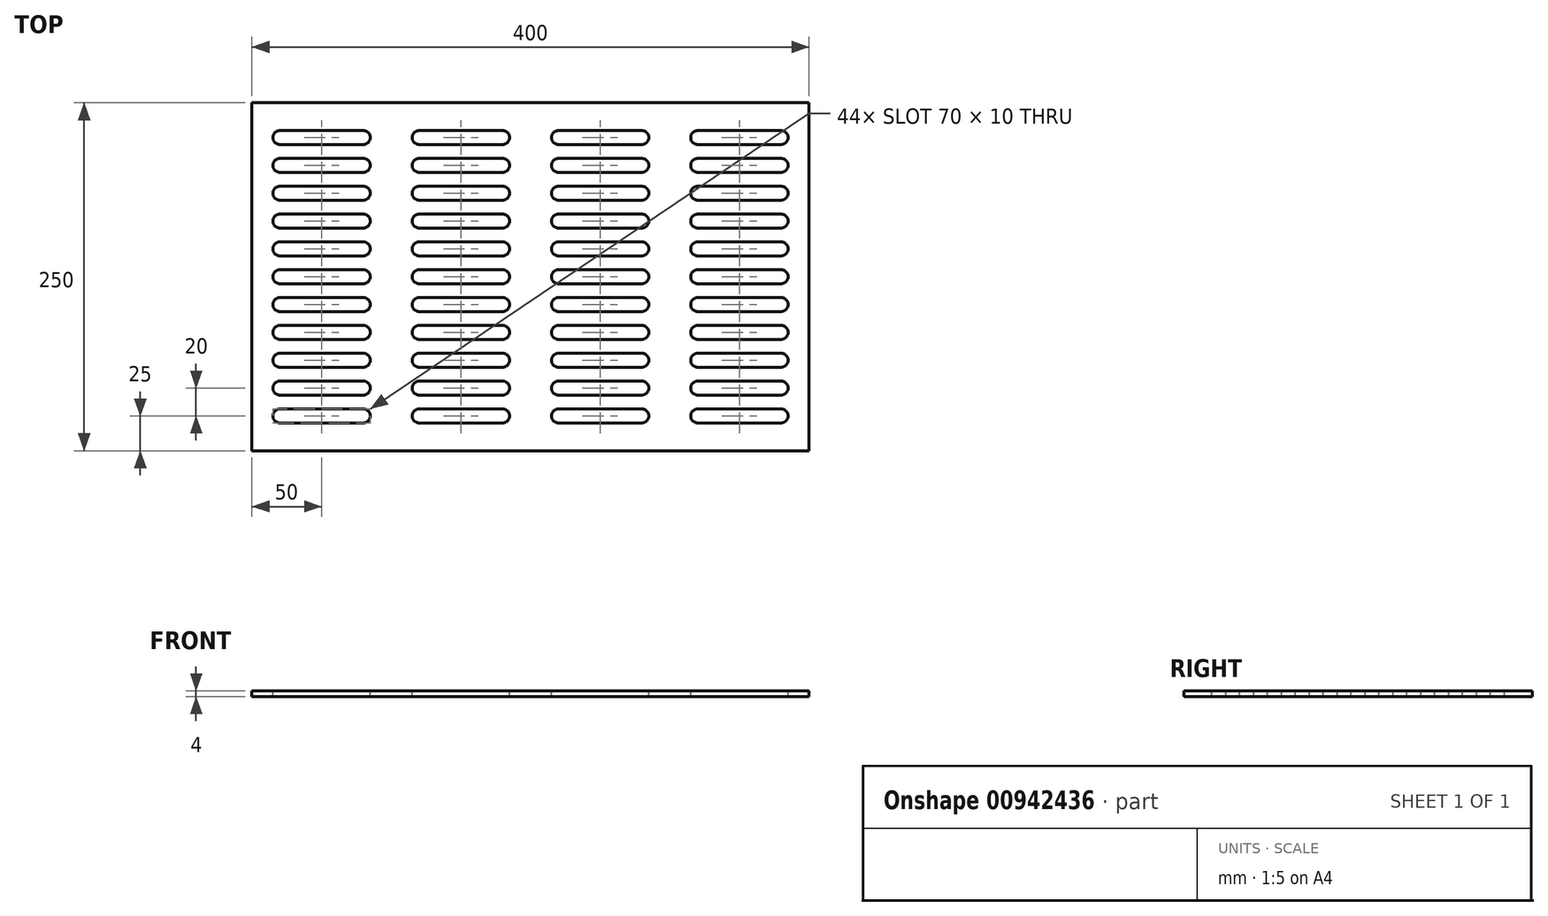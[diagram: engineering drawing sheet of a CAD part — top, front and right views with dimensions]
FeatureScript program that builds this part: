
annotation { "Feature Type Name" : "Feature", "Feature Type Description" : "" }
export const myFeature = defineFeature(function(context is Context, id is Id, definition is map)
    precondition{}
    {
        {
            var Q0;
            Q0=qCreatedBy(makeId("Top.planeOp"),FACE);
            var sketch = newSketch(context, id + "F0", { "sketchPlane" : qUnion([Q0])});
            skLineSegment(sketch, "E0.bottom", {"start": v(-200, 125) * mm, "end": v(200, 125) * mm});
            skLineSegment(sketch, "E0.top", {"start": v(-200, -125) * mm, "end": v(200, -125) * mm});
            skLineSegment(sketch, "E0.left", {"start": v(-200, 125) * mm, "end": v(-200, -125) * mm});
            skLineSegment(sketch, "E0.right", {"start": v(200, 125) * mm, "end": v(200, -125) * mm});
            skSolve(sketch);
        }
        {
            var Q0;
            Q0 = qSketchRegion(id + "F0", true);
            extrude(context, id + "F1", {"entities" : qUnion([Q0]), "depth" : 4 * mm, "offsetDistance" : 25 * mm});
        }
        {
            var Q0;
            Q0=makeQuery(id+"F1.opExtrude","CAP_FACE",FACE,{"disambiguationData":[OSD([sQuery(id+"F0.wireOp",EDGE,"E0.bottom"),sQuery(id+"F0.wireOp",EDGE,"E0.top"),sQuery(id+"F0.wireOp",EDGE,"E0.left"),sQuery(id+"F0.wireOp",EDGE,"E0.right")])],"isStart":false});
            var sketch = newSketch(context, id + "F2", { "sketchPlane" : qUnion([Q0])});
            skCircle(sketch, "E1", {"center": v(25, 80) * mm, "radius": 5 * mm});
            skCircle(sketch, "E2", {"center": v(25, -80) * mm, "radius": 5 * mm});
            skLineSegment(sketch, "E3.bottom", {"start": v(-180, 95) * mm, "end": v(105, 95) * mm});
            skLineSegment(sketch, "E3.top", {"start": v(-180, -95) * mm, "end": v(105, -95) * mm});
            skLineSegment(sketch, "E3.left", {"start": v(-180, 95) * mm, "end": v(-180, -95) * mm});
            skLineSegment(sketch, "E3.right", {"start": v(105, 95) * mm, "end": v(105, -95) * mm});
            skSolve(sketch);
        }
        {
            var Q0;
            Q0=makeQuery(id+"F2.imprint","IMPRINT",FACE,{"disambiguationData":[TD([[makeQuery(id+"F2.imprint","IMPRINT",EDGE,{"derivedFrom":sQuery(id+"F2.wireOp",EDGE,"E1")}),-1.0]])]});
            var sketch = newSketch(context, id + "F3", { "sketchPlane" : qUnion([Q0])});
            skLineSegment(sketch, "E4.bottom", {"start": v(120, 105) * mm, "end": v(180, 105) * mm});
            skLineSegment(sketch, "E4.top", {"start": v(120, 95) * mm, "end": v(180, 95) * mm});
            skArc(sketch, "E5", {"start": v(120, 105) * mm, "mid": v(115, 100) * mm, "end": v(120, 95) * mm});
            skArc(sketch, "E6", {"start": v(180, 95) * mm, "mid": v(185, 100) * mm, "end": v(180, 105) * mm});
            skArc(sketch, "E7.0.1.0", {"start": v(120, 85) * mm, "mid": v(115, 80) * mm, "end": v(120, 75) * mm});
            skLineSegment(sketch, "E7.0.1.1", {"start": v(120, 85) * mm, "end": v(180, 85) * mm});
            skLineSegment(sketch, "E7.0.1.2", {"start": v(120, 75) * mm, "end": v(180, 75) * mm});
            skArc(sketch, "E7.0.1.3", {"start": v(180, 75) * mm, "mid": v(185, 80) * mm, "end": v(180, 85) * mm});
            skArc(sketch, "E7.0.2.0", {"start": v(120, 65) * mm, "mid": v(115, 60) * mm, "end": v(120, 55) * mm});
            skLineSegment(sketch, "E7.0.2.1", {"start": v(120, 65) * mm, "end": v(180, 65) * mm});
            skLineSegment(sketch, "E7.0.2.2", {"start": v(120, 55) * mm, "end": v(180, 55) * mm});
            skArc(sketch, "E7.0.2.3", {"start": v(180, 55) * mm, "mid": v(185, 60) * mm, "end": v(180, 65) * mm});
            skArc(sketch, "E7.0.3.0", {"start": v(120, 45) * mm, "mid": v(115, 40) * mm, "end": v(120, 35) * mm});
            skLineSegment(sketch, "E7.0.3.1", {"start": v(120, 45) * mm, "end": v(180, 45) * mm});
            skLineSegment(sketch, "E7.0.3.2", {"start": v(120, 35) * mm, "end": v(180, 35) * mm});
            skArc(sketch, "E7.0.3.3", {"start": v(180, 35) * mm, "mid": v(185, 40) * mm, "end": v(180, 45) * mm});
            skArc(sketch, "E7.0.4.0", {"start": v(120, 25) * mm, "mid": v(115, 20) * mm, "end": v(120, 15) * mm});
            skLineSegment(sketch, "E7.0.4.1", {"start": v(120, 25) * mm, "end": v(180, 25) * mm});
            skLineSegment(sketch, "E7.0.4.2", {"start": v(120, 15) * mm, "end": v(180, 15) * mm});
            skArc(sketch, "E7.0.4.3", {"start": v(180, 15) * mm, "mid": v(185, 20) * mm, "end": v(180, 25) * mm});
            skArc(sketch, "E7.0.5.0", {"start": v(120, 5) * mm, "mid": v(115, 0) * mm, "end": v(120, -5) * mm});
            skLineSegment(sketch, "E7.0.5.1", {"start": v(120, 5) * mm, "end": v(180, 5) * mm});
            skLineSegment(sketch, "E7.0.5.2", {"start": v(120, -5) * mm, "end": v(180, -5) * mm});
            skArc(sketch, "E7.0.5.3", {"start": v(180, -5) * mm, "mid": v(185, 0) * mm, "end": v(180, 5) * mm});
            skArc(sketch, "E7.0.6.0", {"start": v(120, -15) * mm, "mid": v(115, -20) * mm, "end": v(120, -25) * mm});
            skLineSegment(sketch, "E7.0.6.1", {"start": v(120, -15) * mm, "end": v(180, -15) * mm});
            skLineSegment(sketch, "E7.0.6.2", {"start": v(120, -25) * mm, "end": v(180, -25) * mm});
            skArc(sketch, "E7.0.6.3", {"start": v(180, -25) * mm, "mid": v(185, -20) * mm, "end": v(180, -15) * mm});
            skArc(sketch, "E7.0.7.0", {"start": v(120, -35) * mm, "mid": v(115, -40) * mm, "end": v(120, -45) * mm});
            skLineSegment(sketch, "E7.0.7.1", {"start": v(120, -35) * mm, "end": v(180, -35) * mm});
            skLineSegment(sketch, "E7.0.7.2", {"start": v(120, -45) * mm, "end": v(180, -45) * mm});
            skArc(sketch, "E7.0.7.3", {"start": v(180, -45) * mm, "mid": v(185, -40) * mm, "end": v(180, -35) * mm});
            skArc(sketch, "E7.0.8.0", {"start": v(120, -55) * mm, "mid": v(115, -60) * mm, "end": v(120, -65) * mm});
            skLineSegment(sketch, "E7.0.8.1", {"start": v(120, -55) * mm, "end": v(180, -55) * mm});
            skLineSegment(sketch, "E7.0.8.2", {"start": v(120, -65) * mm, "end": v(180, -65) * mm});
            skArc(sketch, "E7.0.8.3", {"start": v(180, -65) * mm, "mid": v(185, -60) * mm, "end": v(180, -55) * mm});
            skArc(sketch, "E7.1.0.0", {"start": v(20, 105) * mm, "mid": v(15, 100) * mm, "end": v(20, 95) * mm});
            skLineSegment(sketch, "E7.1.0.1", {"start": v(20, 105) * mm, "end": v(80, 105) * mm});
            skLineSegment(sketch, "E7.1.0.2", {"start": v(20, 95) * mm, "end": v(80, 95) * mm});
            skArc(sketch, "E7.1.0.3", {"start": v(80, 95) * mm, "mid": v(85, 100) * mm, "end": v(80, 105) * mm});
            skArc(sketch, "E7.1.1.0", {"start": v(20, 85) * mm, "mid": v(15, 80) * mm, "end": v(20, 75) * mm});
            skLineSegment(sketch, "E7.1.1.1", {"start": v(20, 85) * mm, "end": v(80, 85) * mm});
            skLineSegment(sketch, "E7.1.1.2", {"start": v(20, 75) * mm, "end": v(80, 75) * mm});
            skArc(sketch, "E7.1.1.3", {"start": v(80, 75) * mm, "mid": v(85, 80) * mm, "end": v(80, 85) * mm});
            skArc(sketch, "E7.1.2.0", {"start": v(20, 65) * mm, "mid": v(15, 60) * mm, "end": v(20, 55) * mm});
            skLineSegment(sketch, "E7.1.2.1", {"start": v(20, 65) * mm, "end": v(80, 65) * mm});
            skLineSegment(sketch, "E7.1.2.2", {"start": v(20, 55) * mm, "end": v(80, 55) * mm});
            skArc(sketch, "E7.1.2.3", {"start": v(80, 55) * mm, "mid": v(85, 60) * mm, "end": v(80, 65) * mm});
            skArc(sketch, "E7.1.3.0", {"start": v(20, 45) * mm, "mid": v(15, 40) * mm, "end": v(20, 35) * mm});
            skLineSegment(sketch, "E7.1.3.1", {"start": v(20, 45) * mm, "end": v(80, 45) * mm});
            skLineSegment(sketch, "E7.1.3.2", {"start": v(20, 35) * mm, "end": v(80, 35) * mm});
            skArc(sketch, "E7.1.3.3", {"start": v(80, 35) * mm, "mid": v(85, 40) * mm, "end": v(80, 45) * mm});
            skArc(sketch, "E7.1.4.0", {"start": v(20, 25) * mm, "mid": v(15, 20) * mm, "end": v(20, 15) * mm});
            skLineSegment(sketch, "E7.1.4.1", {"start": v(20, 25) * mm, "end": v(80, 25) * mm});
            skLineSegment(sketch, "E7.1.4.2", {"start": v(20, 15) * mm, "end": v(80, 15) * mm});
            skArc(sketch, "E7.1.4.3", {"start": v(80, 15) * mm, "mid": v(85, 20) * mm, "end": v(80, 25) * mm});
            skArc(sketch, "E7.1.5.0", {"start": v(20, 5) * mm, "mid": v(15, 0) * mm, "end": v(20, -5) * mm});
            skLineSegment(sketch, "E7.1.5.1", {"start": v(20, 5) * mm, "end": v(80, 5) * mm});
            skLineSegment(sketch, "E7.1.5.2", {"start": v(20, -5) * mm, "end": v(80, -5) * mm});
            skArc(sketch, "E7.1.5.3", {"start": v(80, -5) * mm, "mid": v(85, 0) * mm, "end": v(80, 5) * mm});
            skArc(sketch, "E7.1.6.0", {"start": v(20, -15) * mm, "mid": v(15, -20) * mm, "end": v(20, -25) * mm});
            skLineSegment(sketch, "E7.1.6.1", {"start": v(20, -15) * mm, "end": v(80, -15) * mm});
            skLineSegment(sketch, "E7.1.6.2", {"start": v(20, -25) * mm, "end": v(80, -25) * mm});
            skArc(sketch, "E7.1.6.3", {"start": v(80, -25) * mm, "mid": v(85, -20) * mm, "end": v(80, -15) * mm});
            skArc(sketch, "E7.1.7.0", {"start": v(20, -35) * mm, "mid": v(15, -40) * mm, "end": v(20, -45) * mm});
            skLineSegment(sketch, "E7.1.7.1", {"start": v(20, -35) * mm, "end": v(80, -35) * mm});
            skLineSegment(sketch, "E7.1.7.2", {"start": v(20, -45) * mm, "end": v(80, -45) * mm});
            skArc(sketch, "E7.1.7.3", {"start": v(80, -45) * mm, "mid": v(85, -40) * mm, "end": v(80, -35) * mm});
            skArc(sketch, "E7.1.8.0", {"start": v(20, -55) * mm, "mid": v(15, -60) * mm, "end": v(20, -65) * mm});
            skLineSegment(sketch, "E7.1.8.1", {"start": v(20, -55) * mm, "end": v(80, -55) * mm});
            skLineSegment(sketch, "E7.1.8.2", {"start": v(20, -65) * mm, "end": v(80, -65) * mm});
            skArc(sketch, "E7.1.8.3", {"start": v(80, -65) * mm, "mid": v(85, -60) * mm, "end": v(80, -55) * mm});
            skArc(sketch, "E7.2.0.0", {"start": v(-80, 105) * mm, "mid": v(-85, 100) * mm, "end": v(-80, 95) * mm});
            skLineSegment(sketch, "E7.2.0.1", {"start": v(-80, 105) * mm, "end": v(-20, 105) * mm});
            skLineSegment(sketch, "E7.2.0.2", {"start": v(-80, 95) * mm, "end": v(-20, 95) * mm});
            skArc(sketch, "E7.2.0.3", {"start": v(-20, 95) * mm, "mid": v(-15, 100) * mm, "end": v(-20, 105) * mm});
            skArc(sketch, "E7.2.1.0", {"start": v(-80, 85) * mm, "mid": v(-85, 80) * mm, "end": v(-80, 75) * mm});
            skLineSegment(sketch, "E7.2.1.1", {"start": v(-80, 85) * mm, "end": v(-20, 85) * mm});
            skLineSegment(sketch, "E7.2.1.2", {"start": v(-80, 75) * mm, "end": v(-20, 75) * mm});
            skArc(sketch, "E7.2.1.3", {"start": v(-20, 75) * mm, "mid": v(-15, 80) * mm, "end": v(-20, 85) * mm});
            skArc(sketch, "E7.2.2.0", {"start": v(-80, 65) * mm, "mid": v(-85, 60) * mm, "end": v(-80, 55) * mm});
            skLineSegment(sketch, "E7.2.2.1", {"start": v(-80, 65) * mm, "end": v(-20, 65) * mm});
            skLineSegment(sketch, "E7.2.2.2", {"start": v(-80, 55) * mm, "end": v(-20, 55) * mm});
            skArc(sketch, "E7.2.2.3", {"start": v(-20, 55) * mm, "mid": v(-15, 60) * mm, "end": v(-20, 65) * mm});
            skArc(sketch, "E7.2.3.0", {"start": v(-80, 45) * mm, "mid": v(-85, 40) * mm, "end": v(-80, 35) * mm});
            skLineSegment(sketch, "E7.2.3.1", {"start": v(-80, 45) * mm, "end": v(-20, 45) * mm});
            skLineSegment(sketch, "E7.2.3.2", {"start": v(-80, 35) * mm, "end": v(-20, 35) * mm});
            skArc(sketch, "E7.2.3.3", {"start": v(-20, 35) * mm, "mid": v(-15, 40) * mm, "end": v(-20, 45) * mm});
            skArc(sketch, "E7.2.4.0", {"start": v(-80, 25) * mm, "mid": v(-85, 20) * mm, "end": v(-80, 15) * mm});
            skLineSegment(sketch, "E7.2.4.1", {"start": v(-80, 25) * mm, "end": v(-20, 25) * mm});
            skLineSegment(sketch, "E7.2.4.2", {"start": v(-80, 15) * mm, "end": v(-20, 15) * mm});
            skArc(sketch, "E7.2.4.3", {"start": v(-20, 15) * mm, "mid": v(-15, 20) * mm, "end": v(-20, 25) * mm});
            skArc(sketch, "E7.2.5.0", {"start": v(-80, 5) * mm, "mid": v(-85, 0) * mm, "end": v(-80, -5) * mm});
            skLineSegment(sketch, "E7.2.5.1", {"start": v(-80, 5) * mm, "end": v(-20, 5) * mm});
            skLineSegment(sketch, "E7.2.5.2", {"start": v(-80, -5) * mm, "end": v(-20, -5) * mm});
            skArc(sketch, "E7.2.5.3", {"start": v(-20, -5) * mm, "mid": v(-15, 0) * mm, "end": v(-20, 5) * mm});
            skArc(sketch, "E7.2.6.0", {"start": v(-80, -15) * mm, "mid": v(-85, -20) * mm, "end": v(-80, -25) * mm});
            skLineSegment(sketch, "E7.2.6.1", {"start": v(-80, -15) * mm, "end": v(-20, -15) * mm});
            skLineSegment(sketch, "E7.2.6.2", {"start": v(-80, -25) * mm, "end": v(-20, -25) * mm});
            skArc(sketch, "E7.2.6.3", {"start": v(-20, -25) * mm, "mid": v(-15, -20) * mm, "end": v(-20, -15) * mm});
            skArc(sketch, "E7.2.7.0", {"start": v(-80, -35) * mm, "mid": v(-85, -40) * mm, "end": v(-80, -45) * mm});
            skLineSegment(sketch, "E7.2.7.1", {"start": v(-80, -35) * mm, "end": v(-20, -35) * mm});
            skLineSegment(sketch, "E7.2.7.2", {"start": v(-80, -45) * mm, "end": v(-20, -45) * mm});
            skArc(sketch, "E7.2.7.3", {"start": v(-20, -45) * mm, "mid": v(-15, -40) * mm, "end": v(-20, -35) * mm});
            skArc(sketch, "E7.2.8.0", {"start": v(-80, -55) * mm, "mid": v(-85, -60) * mm, "end": v(-80, -65) * mm});
            skLineSegment(sketch, "E7.2.8.1", {"start": v(-80, -55) * mm, "end": v(-20, -55) * mm});
            skLineSegment(sketch, "E7.2.8.2", {"start": v(-80, -65) * mm, "end": v(-20, -65) * mm});
            skArc(sketch, "E7.2.8.3", {"start": v(-20, -65) * mm, "mid": v(-15, -60) * mm, "end": v(-20, -55) * mm});
            skArc(sketch, "E7.3.0.0", {"start": v(-180, 105) * mm, "mid": v(-185, 100) * mm, "end": v(-180, 95) * mm});
            skLineSegment(sketch, "E7.3.0.1", {"start": v(-180, 105) * mm, "end": v(-120, 105) * mm});
            skLineSegment(sketch, "E7.3.0.2", {"start": v(-180, 95) * mm, "end": v(-120, 95) * mm});
            skArc(sketch, "E7.3.0.3", {"start": v(-120, 95) * mm, "mid": v(-115, 100) * mm, "end": v(-120, 105) * mm});
            skArc(sketch, "E7.3.1.0", {"start": v(-180, 85) * mm, "mid": v(-185, 80) * mm, "end": v(-180, 75) * mm});
            skLineSegment(sketch, "E7.3.1.1", {"start": v(-180, 85) * mm, "end": v(-120, 85) * mm});
            skLineSegment(sketch, "E7.3.1.2", {"start": v(-180, 75) * mm, "end": v(-120, 75) * mm});
            skArc(sketch, "E7.3.1.3", {"start": v(-120, 75) * mm, "mid": v(-115, 80) * mm, "end": v(-120, 85) * mm});
            skArc(sketch, "E7.3.2.0", {"start": v(-180, 65) * mm, "mid": v(-185, 60) * mm, "end": v(-180, 55) * mm});
            skLineSegment(sketch, "E7.3.2.1", {"start": v(-180, 65) * mm, "end": v(-120, 65) * mm});
            skLineSegment(sketch, "E7.3.2.2", {"start": v(-180, 55) * mm, "end": v(-120, 55) * mm});
            skArc(sketch, "E7.3.2.3", {"start": v(-120, 55) * mm, "mid": v(-115, 60) * mm, "end": v(-120, 65) * mm});
            skArc(sketch, "E7.3.3.0", {"start": v(-180, 45) * mm, "mid": v(-185, 40) * mm, "end": v(-180, 35) * mm});
            skLineSegment(sketch, "E7.3.3.1", {"start": v(-180, 45) * mm, "end": v(-120, 45) * mm});
            skLineSegment(sketch, "E7.3.3.2", {"start": v(-180, 35) * mm, "end": v(-120, 35) * mm});
            skArc(sketch, "E7.3.3.3", {"start": v(-120, 35) * mm, "mid": v(-115, 40) * mm, "end": v(-120, 45) * mm});
            skArc(sketch, "E7.3.4.0", {"start": v(-180, 25) * mm, "mid": v(-185, 20) * mm, "end": v(-180, 15) * mm});
            skLineSegment(sketch, "E7.3.4.1", {"start": v(-180, 25) * mm, "end": v(-120, 25) * mm});
            skLineSegment(sketch, "E7.3.4.2", {"start": v(-180, 15) * mm, "end": v(-120, 15) * mm});
            skArc(sketch, "E7.3.4.3", {"start": v(-120, 15) * mm, "mid": v(-115, 20) * mm, "end": v(-120, 25) * mm});
            skArc(sketch, "E7.3.5.0", {"start": v(-180, 5) * mm, "mid": v(-185, 0) * mm, "end": v(-180, -5) * mm});
            skLineSegment(sketch, "E7.3.5.1", {"start": v(-180, 5) * mm, "end": v(-120, 5) * mm});
            skLineSegment(sketch, "E7.3.5.2", {"start": v(-180, -5) * mm, "end": v(-120, -5) * mm});
            skArc(sketch, "E7.3.5.3", {"start": v(-120, -5) * mm, "mid": v(-115, 0) * mm, "end": v(-120, 5) * mm});
            skArc(sketch, "E7.3.6.0", {"start": v(-180, -15) * mm, "mid": v(-185, -20) * mm, "end": v(-180, -25) * mm});
            skLineSegment(sketch, "E7.3.6.1", {"start": v(-180, -15) * mm, "end": v(-120, -15) * mm});
            skLineSegment(sketch, "E7.3.6.2", {"start": v(-180, -25) * mm, "end": v(-120, -25) * mm});
            skArc(sketch, "E7.3.6.3", {"start": v(-120, -25) * mm, "mid": v(-115, -20) * mm, "end": v(-120, -15) * mm});
            skArc(sketch, "E7.3.7.0", {"start": v(-180, -35) * mm, "mid": v(-185, -40) * mm, "end": v(-180, -45) * mm});
            skLineSegment(sketch, "E7.3.7.1", {"start": v(-180, -35) * mm, "end": v(-120, -35) * mm});
            skLineSegment(sketch, "E7.3.7.2", {"start": v(-180, -45) * mm, "end": v(-120, -45) * mm});
            skArc(sketch, "E7.3.7.3", {"start": v(-120, -45) * mm, "mid": v(-115, -40) * mm, "end": v(-120, -35) * mm});
            skArc(sketch, "E7.3.8.0", {"start": v(-180, -55) * mm, "mid": v(-185, -60) * mm, "end": v(-180, -65) * mm});
            skLineSegment(sketch, "E7.3.8.1", {"start": v(-180, -55) * mm, "end": v(-120, -55) * mm});
            skLineSegment(sketch, "E7.3.8.2", {"start": v(-180, -65) * mm, "end": v(-120, -65) * mm});
            skArc(sketch, "E7.3.8.3", {"start": v(-120, -65) * mm, "mid": v(-115, -60) * mm, "end": v(-120, -55) * mm});
            skLineSegment(sketch, "E7.direction1", {"start": v(120, 100) * mm, "end": v(20, 100) * mm, "construction": true});
            skLineSegment(sketch, "E7.direction2", {"start": v(120, 100) * mm, "end": v(120, 80) * mm, "construction": true});
            skArc(sketch, "E8.0.0.9", {"start": v(120, -75) * mm, "mid": v(115, -80) * mm, "end": v(120, -85) * mm});
            skLineSegment(sketch, "E8.4.0.9", {"start": v(120, -75) * mm, "end": v(180, -75) * mm});
            skLineSegment(sketch, "E8.7.0.9", {"start": v(120, -85) * mm, "end": v(180, -85) * mm});
            skArc(sketch, "E8.10.0.9", {"start": v(180, -85) * mm, "mid": v(185, -80) * mm, "end": v(180, -75) * mm});
            skArc(sketch, "E8.0.0.10", {"start": v(120, -95) * mm, "mid": v(115, -100) * mm, "end": v(120, -105) * mm});
            skLineSegment(sketch, "E8.4.0.10", {"start": v(120, -95) * mm, "end": v(180, -95) * mm});
            skLineSegment(sketch, "E8.7.0.10", {"start": v(120, -105) * mm, "end": v(180, -105) * mm});
            skArc(sketch, "E8.10.0.10", {"start": v(180, -105) * mm, "mid": v(185, -100) * mm, "end": v(180, -95) * mm});
            skArc(sketch, "E8.0.1.9", {"start": v(20, -75) * mm, "mid": v(15, -80) * mm, "end": v(20, -85) * mm});
            skLineSegment(sketch, "E8.4.1.9", {"start": v(20, -75) * mm, "end": v(80, -75) * mm});
            skLineSegment(sketch, "E8.7.1.9", {"start": v(20, -85) * mm, "end": v(80, -85) * mm});
            skArc(sketch, "E8.10.1.9", {"start": v(80, -85) * mm, "mid": v(85, -80) * mm, "end": v(80, -75) * mm});
            skArc(sketch, "E8.0.1.10", {"start": v(20, -95) * mm, "mid": v(15, -100) * mm, "end": v(20, -105) * mm});
            skLineSegment(sketch, "E8.4.1.10", {"start": v(20, -95) * mm, "end": v(80, -95) * mm});
            skLineSegment(sketch, "E8.7.1.10", {"start": v(20, -105) * mm, "end": v(80, -105) * mm});
            skArc(sketch, "E8.10.1.10", {"start": v(80, -105) * mm, "mid": v(85, -100) * mm, "end": v(80, -95) * mm});
            skArc(sketch, "E8.0.2.9", {"start": v(-80, -75) * mm, "mid": v(-85, -80) * mm, "end": v(-80, -85) * mm});
            skLineSegment(sketch, "E8.4.2.9", {"start": v(-80, -75) * mm, "end": v(-20, -75) * mm});
            skLineSegment(sketch, "E8.7.2.9", {"start": v(-80, -85) * mm, "end": v(-20, -85) * mm});
            skArc(sketch, "E8.10.2.9", {"start": v(-20, -85) * mm, "mid": v(-15, -80) * mm, "end": v(-20, -75) * mm});
            skArc(sketch, "E8.0.2.10", {"start": v(-80, -95) * mm, "mid": v(-85, -100) * mm, "end": v(-80, -105) * mm});
            skLineSegment(sketch, "E8.4.2.10", {"start": v(-80, -95) * mm, "end": v(-20, -95) * mm});
            skLineSegment(sketch, "E8.7.2.10", {"start": v(-80, -105) * mm, "end": v(-20, -105) * mm});
            skArc(sketch, "E8.10.2.10", {"start": v(-20, -105) * mm, "mid": v(-15, -100) * mm, "end": v(-20, -95) * mm});
            skArc(sketch, "E8.0.3.9", {"start": v(-180, -75) * mm, "mid": v(-185, -80) * mm, "end": v(-180, -85) * mm});
            skLineSegment(sketch, "E8.4.3.9", {"start": v(-180, -75) * mm, "end": v(-120, -75) * mm});
            skLineSegment(sketch, "E8.7.3.9", {"start": v(-180, -85) * mm, "end": v(-120, -85) * mm});
            skArc(sketch, "E8.10.3.9", {"start": v(-120, -85) * mm, "mid": v(-115, -80) * mm, "end": v(-120, -75) * mm});
            skArc(sketch, "E8.0.3.10", {"start": v(-180, -95) * mm, "mid": v(-185, -100) * mm, "end": v(-180, -105) * mm});
            skLineSegment(sketch, "E8.4.3.10", {"start": v(-180, -95) * mm, "end": v(-120, -95) * mm});
            skLineSegment(sketch, "E8.7.3.10", {"start": v(-180, -105) * mm, "end": v(-120, -105) * mm});
            skArc(sketch, "E8.10.3.10", {"start": v(-120, -105) * mm, "mid": v(-115, -100) * mm, "end": v(-120, -95) * mm});
            skSolve(sketch);
        }
        {
            var Q0;
            Q0 = qSketchRegion(id + "F3", true);
            extrude(context, id + "F4", {"entities" : qUnion([Q0]), "operationType" : NewBodyOperationType.REMOVE, "oppositeDirection" : true, "depth" : 25 * mm, "offsetDistance" : 25 * mm});
        }
    });
